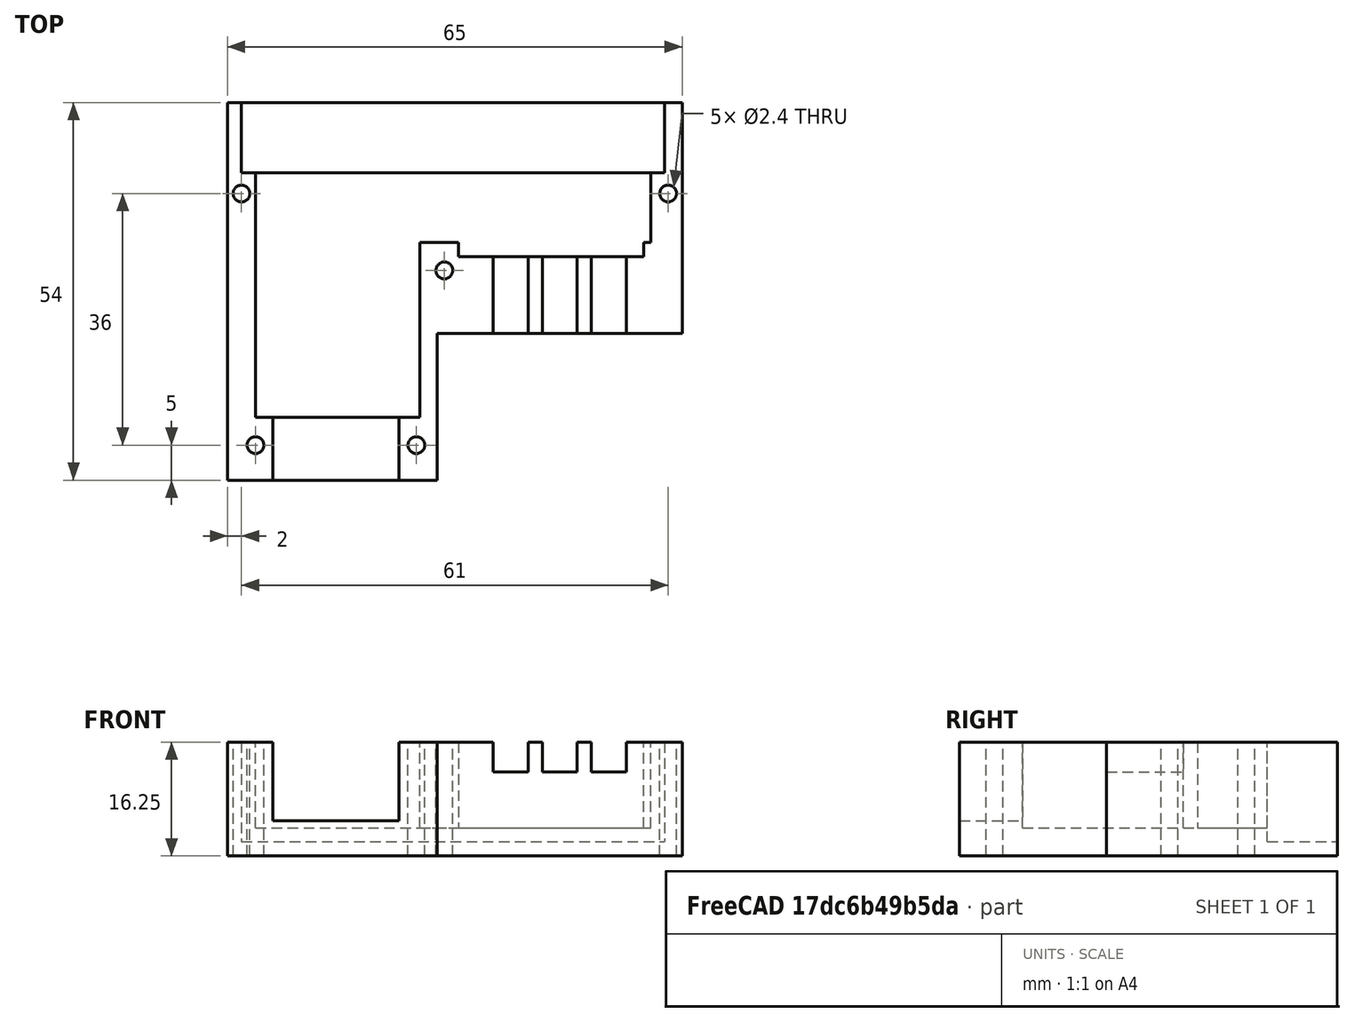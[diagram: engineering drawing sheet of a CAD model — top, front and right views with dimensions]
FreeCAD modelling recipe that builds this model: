
FCSTD DOCUMENT  (FreeCAD 0.15R4671 (Git))
Label: cablein
License: All rights reserved
LicenseURL: http://en.wikipedia.org/wiki/All_rights_reserved
objects: Part::Box×10, Part::Cylinder×6, Part::MultiFuse×2, Part::Cut×1, Mesh::Feature×1
note: 19 computed .brp shape members not serialized (recipe doc carries the construction recipe); baked Part::Feature solids carry a one-line shape summary decoded from their .brp

FEATURE [Part::Box] Box  label="Cube"
  Height = 14.25
  Length = 60.5
  Placement = pos=(2,12,2) rot=(0,0,1;0rad)
  Width = 12
FEATURE [Part::Box] Box001  label="Cube001"
  Height = 16.25
  Length = 65
  Placement = pos=(0,-11,0) rot=(0,0,1;0rad)
  Width = 33
FEATURE [Part::Box] Box002  label="Cube002"
  Height = 12.25
  Length = 56.5
  Placement = pos=(4,2,4) rot=(0,0,1;0rad)
  Width = 10
FEATURE [Part::Box] Box003  label="Cube003"
  Height = 16.25
  Length = 30
  Placement = pos=(0,-32,0) rot=(0,0,1;0rad)
  Width = 30
FEATURE [Part::Box] Box004  label="Cube004"
  Height = 12.25
  Length = 23.5
  Placement = pos=(4,-23,4) rot=(0,0,1;0rad)
  Width = 26
FEATURE [Part::Cylinder] Cylinder
  Angle = 360
  Height = 14
  Placement = pos=(17.5,-22,16.25) rot=(1,0,0;1.5708rad)
  Radius = 5
FEATURE [Part::Box] Box005  label="Cube005"
  Height = 12.25
  Length = 26.5
  Placement = pos=(33,0,4) rot=(0,0,1;0rad)
  Width = 7
FEATURE [Part::Box] Box006  label="Cube006"
  Height = 4.25
  Length = 5
  Placement = pos=(38,-11,12) rot=(0,0,1;0rad)
  Width = 19
FEATURE [Part::Box] Box007  label="Cube007"
  Height = 4.25
  Length = 5
  Placement = pos=(45,-11,12) rot=(0,0,1;0rad)
  Width = 19
FEATURE [Part::Box] Box008  label="Cube008"
  Height = 4.25
  Length = 5
  Placement = pos=(52,-11,12) rot=(0,0,1;0rad)
  Width = 19
FEATURE [Part::MultiFuse] Fusion
  Shapes = -> [Box003,Box001]
FEATURE [Part::Cylinder] Cylinder001
  Angle = 360
  Height = 27
  Placement = pos=(2,9,-4) rot=(0,0,1;0rad)
  Radius = 1.2
FEATURE [Part::Cylinder] Cylinder002
  Angle = 360
  Height = 27
  Placement = pos=(4,-27,-4) rot=(0,0,1;0rad)
  Radius = 1.2
FEATURE [Part::Cylinder] Cylinder003
  Angle = 360
  Height = 27
  Placement = pos=(27,-27,-4) rot=(0,0,1;0rad)
  Radius = 1.2
FEATURE [Part::Cylinder] Cylinder004
  Angle = 360
  Height = 27
  Placement = pos=(31,-2,-4) rot=(0,0,1;0rad)
  Radius = 1.2
FEATURE [Part::Cylinder] Cylinder005
  Angle = 360
  Height = 27
  Placement = pos=(63,9,-4) rot=(0,0,1;0rad)
  Radius = 1.2
FEATURE [Part::Box] Box009  label="Cube009"
  Height = 12
  Length = 18
  Placement = pos=(6.5,-35,5) rot=(0,0,1;0rad)
  Width = 15
FEATURE [Part::MultiFuse] Fusion001
  Shapes = -> [Cylinder001,Box,Box002,Box004,Cylinder,Box006,Box005,Box007,Box008,Cylinder002,Cylinder003,Cylinder004,Cylinder005,Box009]
FEATURE [Part::Cut] Cut
  Base = -> Fusion
  Tool = -> Fusion001
FEATURE [Mesh::Feature] Mesh  label="Cut (Meshed)"
